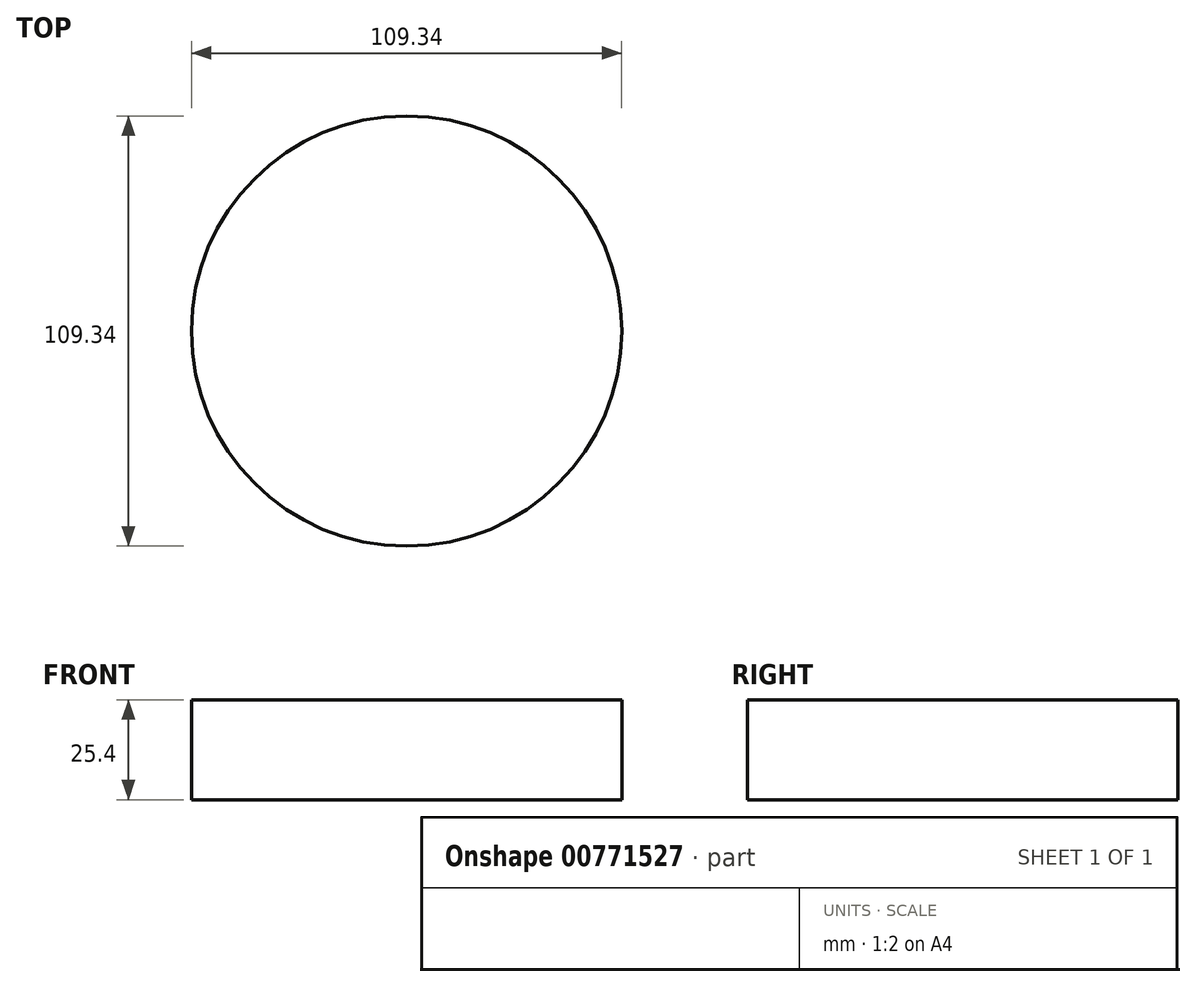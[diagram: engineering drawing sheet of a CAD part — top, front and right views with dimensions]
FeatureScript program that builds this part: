
annotation { "Feature Type Name" : "Feature", "Feature Type Description" : "" }
export const myFeature = defineFeature(function(context is Context, id is Id, definition is map)
    precondition{}
    {
        {
            var Q0;
            Q0=qCreatedBy(makeId("Top.planeOp"),FACE);
            var sketch = newSketch(context, id + "F0", { "sketchPlane" : qUnion([Q0])});
            skCircle(sketch, "E0", {"center": v(0, 0) * mm, "radius": 54.67 * mm});
            skSolve(sketch);
        }
        {
            var Q0;
            Q0=sQuery(id+"F0.wireOp",EDGE,"E0");
            extrude(context, id + "F1", {"bodyType" : ToolBodyType.SURFACE, "surfaceEntities" : qUnion([Q0]), "depth" : 25.4 * mm, "offsetDistance" : 25.4 * mm});
        }
    });
